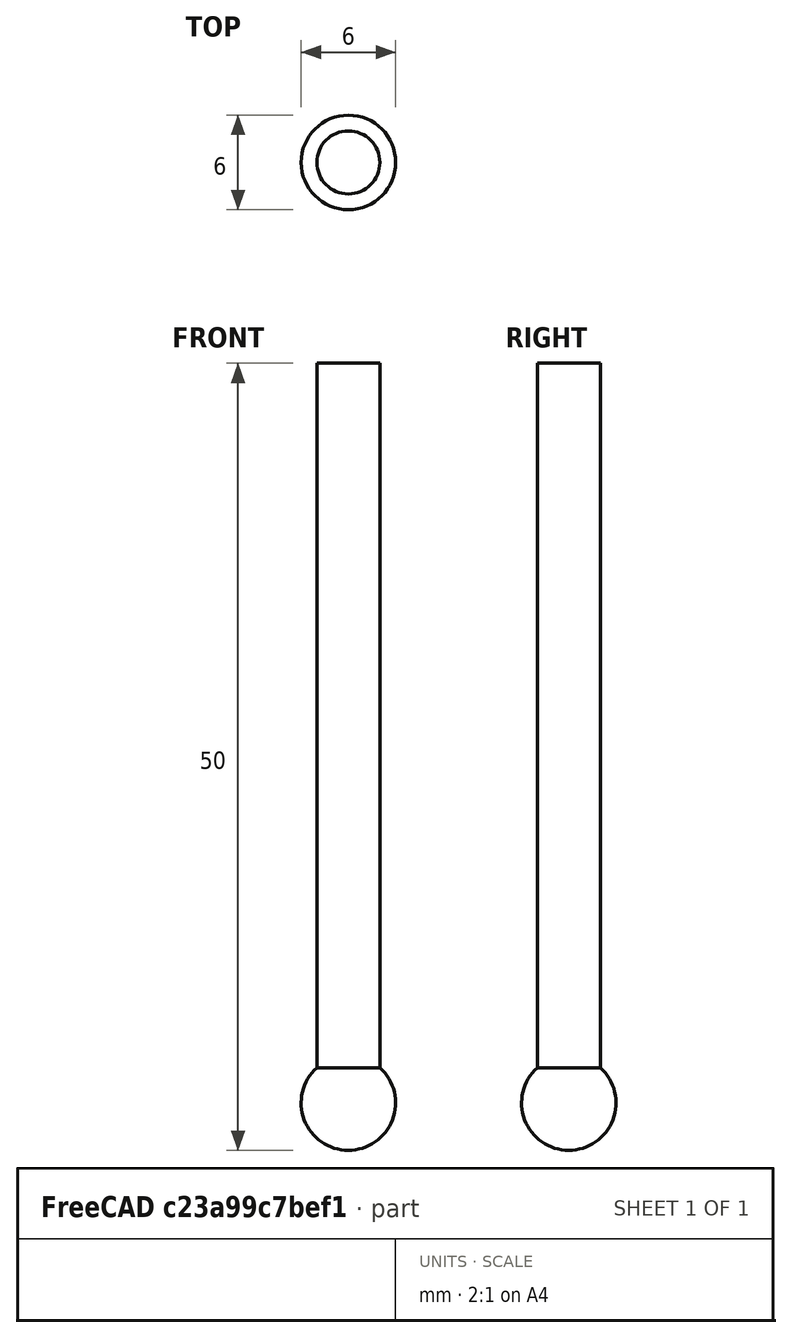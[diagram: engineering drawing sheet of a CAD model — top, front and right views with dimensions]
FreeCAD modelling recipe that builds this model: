
FCSTD DOCUMENT  (FreeCAD 0.19R24049 (Git))
Label: probe
License: All rights reserved
LicenseURL: http://en.wikipedia.org/wiki/All_rights_reserved
objects: Sketcher::SketchObject×1, PartDesign::Revolution×1, App::FeaturePython×1, PartDesign::Body×1
note: 4 computed .brp shape members not serialized (recipe doc carries the construction recipe); baked Part::Feature solids carry a one-line shape summary decoded from their .brp

FEATURE [Sketcher::SketchObject] Sketch
  FullyConstrained = true
  MapMode = 5
  Placement = pos=(0,0,0) rot=(1,0,0;1.5708rad)
  Support = -> [XZ_Plane]
  expr: Constraints[11] = <<Attributes>>.Diameter
  expr: Constraints[15] = <<Attributes>>.Length
  expr: Constraints[8] = <<Attributes>>.ShaftDiameter
  sketch-geometry (6):
    g0: LineSegment StartX=-6e-16 StartY=0 StartZ=0 EndX=2 EndY=0 EndZ=0
    g1: LineSegment StartX=2 StartY=0 StartZ=0 EndX=2 EndY=-44.7639 EndZ=0
    g2: LineSegment StartX=-6e-16 StartY=-50 StartZ=0 EndX=-6e-16 EndY=0 EndZ=0
    g3: LineSegment StartX=-2 StartY=0 StartZ=0 EndX=2 EndY=0 EndZ=0
    g4: ArcOfCircle CenterX=0 CenterY=-47 CenterZ=0 NormalX=0 NormalY=0 NormalZ=1 AngleXU=0 Radius=3 StartAngle=4.71239 EndAngle=7.12425
    g5: LineSegment StartX=0 StartY=-47 StartZ=0 EndX=0 EndY=-53 EndZ=0
  constraints (16):
    c: Coincident(g0,g1)
    c: Coincident(g2,g0)
    c: Horizontal(g0)
    c: Vertical(g1)
    c: Vertical(g2)
    c: Coincident(g0,g-1)
    c: Symmetric(g3,g3,g-2)
    c: Coincident(g0,g3)
    c: DistanceX(g3,g3) = 4
    c: PointOnObject(g4,g2)
    c: Coincident(g4,g2)
    c: DistanceY(g5,g5) = 6
    c: Coincident(g5,g4)
    c: Coincident(g4,g1)
    c: Symmetric(g4,g5,g2)
    c: DistanceY(g2,g2) = 50
FEATURE [PartDesign::Revolution] Revolution
  AllowMultiFace = false
  Angle = 360
  Axis = (0,-2e-16,1)
  Base = (0,0,0)
  Placement = pos=(0,0,0) rot=(1,0,0;1.5708rad)
  Profile = -> Sketch
  ReferenceAxis = -> Sketch [V_Axis]
  Reversed = true
FEATURE [App::FeaturePython] PropertyBag  label="Attributes"  # WARN: FeaturePython — macro-defined, semantics opaque (R4)
  CustomPropertyGroups = Shape | Attributes
  Diameter = 6
  Length = 50
  ShaftDiameter = 4
  SpindlePower = false
FEATURE [PartDesign::Body] Body  label="Probe"
  Group = -> [Sketch,Revolution,PropertyBag]
  Origin = -> Origin
  Tip = -> Revolution
